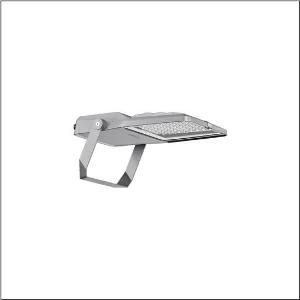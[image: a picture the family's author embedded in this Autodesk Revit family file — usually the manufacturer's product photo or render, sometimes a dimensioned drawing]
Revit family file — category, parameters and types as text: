
# Revit family: floodlight_fl_21_iq_mini___pl33t_5xa7772c2f1a_05f5
name_source: partatom
category: Lighting Fixtures
units: mm (PartAtom-declared; Revit-internal decimal feet)

## family parameters
Cut with Voids When Loaded = No
Host = Face
Light Source = No
Part Type = Normal
Room Calculation Point = No
Round Connector Dimension = Use Diameter
Shared = No

## types (1)
- --- (1 x LED, 12060 lm, 87.2 W, 3000K)
    Apparent Load = 87 VA
    CIE Flux Codes = 26 75 99 100 100
    Color Rendering = 70
    Color Temperature = 3000K
    Default Elevation = 1800 mm
    Description = Floodlight FL 21 iQ mini, floodlight, primary light control with lens, of PMMA, primary optical cover: protective disc, of toughened safety glass, transparent, light distribution: PL33T, light emission: direct distribution, installation type: surface-mounted, LED, High Power LED, rated luminous flux: 12.060lm, luminous efficacy: 138lm/W, light colour: 730, colour temperature: 3000K, control: Street-Remote, Auto-Match, Temp-Guard, Night-Set, Smart-Wire, Desk-Remote (wireless, voltage-free reading and setting of iQ features in the workshop via application-optimized NFC function/RFID function), optimised constant luminous flux control (CLO 2.0), with terminal, 6-pole, mains connection: 220..240V, AC, 50/60Hz, start of lifetime: 87W, end of service life: 92W, reduction: 40W, luminaire housing, of diecast aluminium, powder-coated, Siteco® metallic grey (DB 702S), corrosivity category C5 mid according to DIN EN ISO 12944, sealing non-destructively replaceable, mounting bracket, of steel, galvanised, powder-coated, Siteco® metallic grey (DB 702S), protection rating (complete): IP66, insulation class (complete): insulation class II (safety insulation), certification: CE, ENEC, VDE, protection symbol: D, impact resistance: IK08, permissible operating ambient temperature: -40..+40°C, permissible operating ambient temperature for outdoor applications: -40..+50°C, standard: DIN EN 12944, LABS conformity tested according to VDMA 24364:2018-05, packaging unit: 1 piece

Light Distribution: PL33T
    Height = 70 mm
    Lamp = 1 x LED
    Lamp Light Flux = 12060 lm
    Lamp Power = 87.2 W
    Lamp count = 1
    Length = 485 mm
    Luminous efficacy = 138 lm/W
    Manufacturer = Siteco
    ModVariant = No
    Model = 5XA7772C2F1A
    Number of Poles = 1
    OnlyDefault = Yes
    Power Factor = 1
    Product Name = Floodlight FL 21 iQ mini | PL33T
    Product group = floodlight | pylon annexe
    ProductGroupID = 6200
    Protection Class = Protection class II
    Protection Degree = IP 66
    RLX_Detail_Level = 1
    RLX_Emergency_Light_Flux = 0 lm
    RLX_Emergency_Type = 0
    RLX_Emergency_Type_DB = No
    RlxData = <blob elided: 96125 chars, md5=41b76e3f>
    Socket = socket
    Standby Power = 0 W
    System Light Flux = 12060 lm
    System Power = 87 W
    Type Comments = factory setting: luminous flux: 100 % | dim-lin: 254 | 456 mA
    Type Image = l_1006845.jpg
    URL = http://relux.com
    VarID = @adj_082047
    Voltage = 0 V
    Weight = 0.00 kg
    Width = 337 mm

## geometry (parser evidence)
native form markers: Blend x4, Sweep x12
no freeform markers — native parametric forms only
